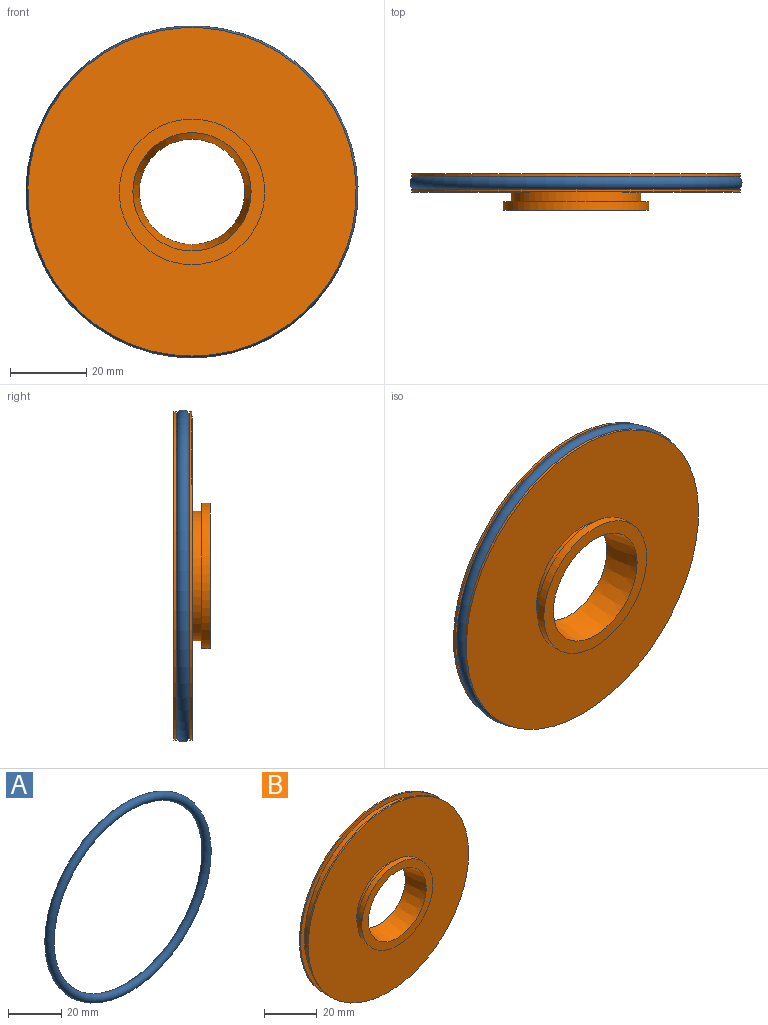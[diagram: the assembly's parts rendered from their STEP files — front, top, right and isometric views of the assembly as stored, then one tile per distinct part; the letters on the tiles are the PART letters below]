
ASSEMBLY  parts=2 mates=1
PART A: 1 faces, bbox 94.2x3.5x94.2 mm
  f0: torus R=41.75mm, axis (0,-1,0), area 2884.4mm2
PART B: 12 faces, bbox 86x9.5x86 mm
  f0: plane 86x86mm, normal (0,-1,0), area 4900.9mm2, adj f1,f11
  f1: cylinder r=17mm len=34mm, axis (0,-1,0), area 267mm2, adj f0,f2
  f2: plane 38.1x38.1mm, normal (0,1,0), area 232.2mm2, adj f1,f3
  f3: cylinder r=19.05mm len=38.1mm, axis (0,-1,0), area 270.8mm2, adj f2,f4
  f4: plane 38.1x38.1mm, normal (0,-1,0), area 386.7mm2, adj f3,f5
  f5: cone r=15.49mm half-angle=10deg, axis (0,-1,0), area 890.1mm2, adj f4,f6
  f6: plane 86x86mm, normal (0,1,0), area 5210mm2, adj f5,f7
  f7: cylinder r=43mm len=86mm, axis (0,-1,0), area 170.5mm2, adj f6,f8
  f8: plane 86x86mm, normal (0,-1,0), area 527.8mm2, adj f7,f9
  f9: cylinder r=41mm len=82mm, axis (0,-1,0), area 901.6mm2, adj f8,f10
  f10: plane 86x86mm, normal (0,1,0), area 527.8mm2, adj f9,f11
  f11: cylinder r=43mm len=86mm, axis (0,-1,0), area 170.6mm2, adj f0,f10
PLACE A t=(-6.77,-8.2,-9.74)mm
PLACE B t=(-6.77,-5.81,-10)mm
MATE ball A.f0 <-> B.f5  axis (0,-1,0) through (-6.77,-8.2,-10)mm
